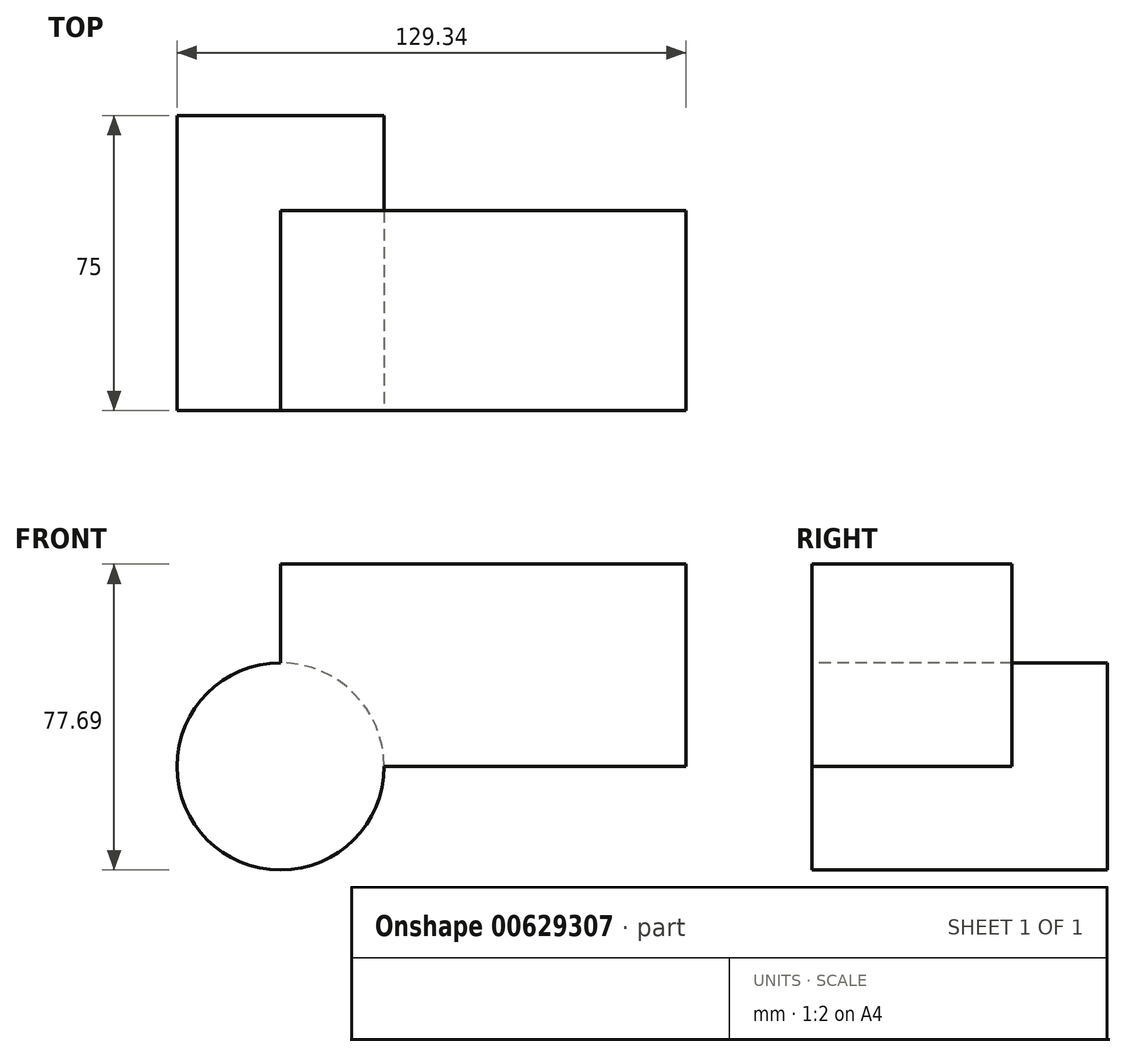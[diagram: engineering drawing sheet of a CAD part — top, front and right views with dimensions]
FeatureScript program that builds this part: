
annotation { "Feature Type Name" : "Feature", "Feature Type Description" : "" }
export const myFeature = defineFeature(function(context is Context, id is Id, definition is map)
    precondition{}
    {
        {
            var Q0;
            Q0=qCreatedBy(makeId("Front.planeOp"),FACE);
            var sketch = newSketch(context, id + "F0", { "sketchPlane" : qUnion([Q0])});
            skLineSegment(sketch, "E0.bottom", {"start": v(0, 0) * mm, "end": v(103.03, 0) * mm});
            skLineSegment(sketch, "E0.top", {"start": v(0, 51.38) * mm, "end": v(103.03, 51.38) * mm});
            skLineSegment(sketch, "E0.left", {"start": v(0, 0) * mm, "end": v(0, 51.38) * mm});
            skLineSegment(sketch, "E0.right", {"start": v(103.03, 0) * mm, "end": v(103.03, 51.38) * mm});
            skSolve(sketch);
        }
        {
            var Q0;
            Q0 = qSketchRegion(id + "F0", true);
            extrude(context, id + "F1", {"entities" : qUnion([Q0]), "depth" : 50.8 * mm, "offsetDistance" : 25.4 * mm});
        }
        {
            var Q0;
            Q0=makeQuery(id+"F1.opExtrude","CAP_FACE",FACE,{"disambiguationData":[OSD([sQuery(id+"F0.wireOp",EDGE,"E0.bottom"),sQuery(id+"F0.wireOp",EDGE,"E0.top"),sQuery(id+"F0.wireOp",EDGE,"E0.left"),sQuery(id+"F0.wireOp",EDGE,"E0.right")])],"isStart":false});
            var sketch = newSketch(context, id + "F2", { "sketchPlane" : qUnion([Q0])});
            skCircle(sketch, "E1", {"center": v(0, 0) * mm, "radius": 26.31 * mm});
            skSolve(sketch);
        }
        {
            var Q0;
            Q0 = qSketchRegion(id + "F2", true);
            extrude(context, id + "F3", {"entities" : qUnion([Q0]), "operationType" : NewBodyOperationType.ADD, "oppositeDirection" : true, "depth" : 75 * mm, "offsetDistance" : 25 * mm});
        }
    });
